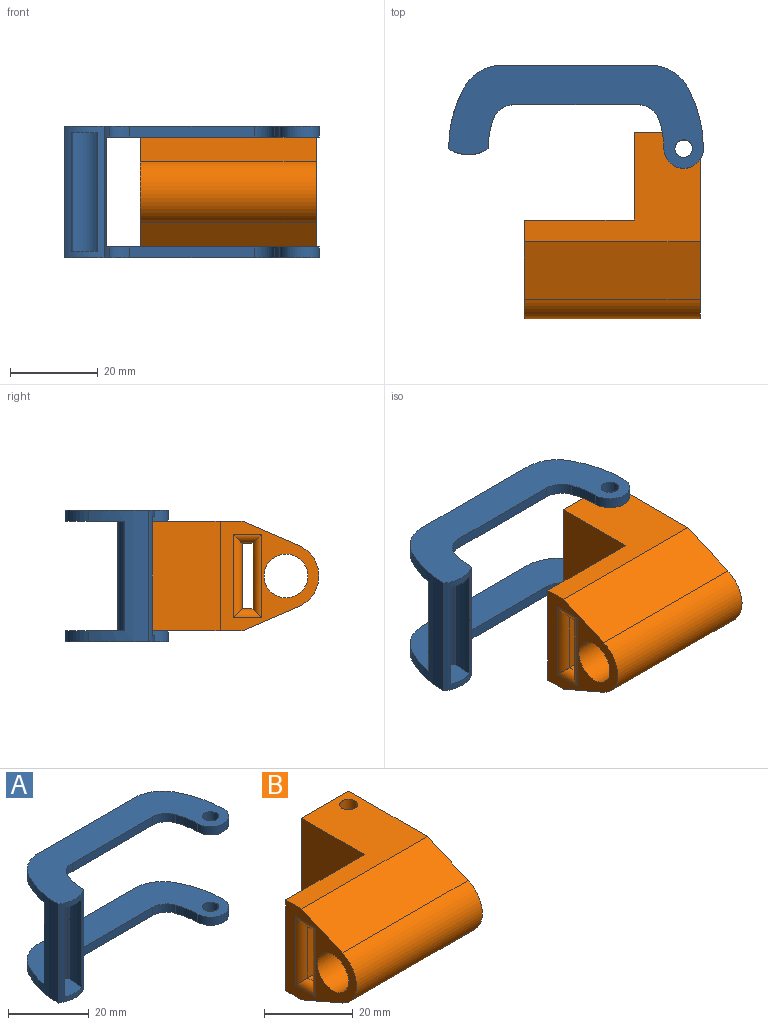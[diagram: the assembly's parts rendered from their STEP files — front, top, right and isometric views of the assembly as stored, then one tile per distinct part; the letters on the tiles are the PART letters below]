
ASSEMBLY  parts=2 mates=1
PART A: 33 faces, bbox 58x23.5x30 mm
  f0: cylinder r=8mm len=30mm, axis (0,0,-1), area 120.6mm2, adj f4,f7,f8,f12,f29,f30,f31,f32
  f1: cylinder r=6mm len=25mm, axis (0,0,-1), area 255.4mm2, adj f2,f7,f8,f19
  f2: plane 57.47x23.5mm, normal (0,0,1), area 591mm2, adj f1,f3,f5,f6,f7,f8,f9,f10
  f3: cylinder r=2mm len=4mm, axis (0,0,-1), area 31.4mm2, adj f2,f4
  f4: plane 58x23.5mm, normal (0,0,-1), area 656.9mm2, adj f0,f3,f5,f6,f7,f8,f9,f10
  f5: cylinder r=20mm len=6.67mm, axis (0,0,-1), area 17mm2, adj f2,f4,f11,f25
  f6: plane 28.28x2.5mm, normal (0,-1,0), area 70.7mm2, adj f2,f4,f24,f25
  f7: cylinder r=20mm len=30mm, axis (0,0,-1), area 143.6mm2, adj f0,f1,f2,f4,f12,f19,f24,f26
  f8: cylinder r=29mm len=30mm, axis (0,0,-1), area 209.8mm2, adj f0,f1,f2,f4,f12,f19,f21,f23
  f9: plane 33.47x2.5mm, normal (0,1,0), area 83.7mm2, adj f2,f4,f20,f21
  f10: cylinder r=29mm len=13.74mm, axis (0,0,-1), area 35.8mm2, adj f2,f4,f11,f20
  f11: cylinder r=4.5mm len=9mm, axis (0,0,-1), area 35.3mm2, adj f2,f4,f5,f10
  f12: plane 58x23.5mm, normal (0,0,1), area 656.9mm2, adj f0,f7,f8,f13,f14,f15,f16,f17
  f13: cylinder r=4.5mm len=9mm, axis (0,0,-1), area 35.3mm2, adj f12,f14,f18,f19
  f14: cylinder r=29mm len=13.74mm, axis (0,0,-1), area 35.8mm2, adj f12,f13,f19,f22
  f15: plane 33.47x2.5mm, normal (0,1,0), area 83.7mm2, adj f12,f19,f22,f23
  f16: plane 28.28x2.5mm, normal (0,-1,0), area 70.7mm2, adj f12,f19,f26,f27
  f17: cylinder r=2mm len=4mm, axis (0,0,-1), area 31.4mm2, adj f12,f19
  f18: cylinder r=20mm len=6.67mm, axis (0,0,-1), area 17mm2, adj f12,f13,f19,f27
  f19: plane 57.47x23.5mm, normal (0,0,-1), area 591mm2, adj f1,f7,f8,f13,f14,f15,f16,f17
  f20: cylinder r=10mm len=8.81mm, axis (0,0,-1), area 26.9mm2, adj f2,f4,f9,f10
  f21: cylinder r=10mm len=8.81mm, axis (0,0,-1), area 26.9mm2, adj f2,f4,f8,f9
  f22: cylinder r=10mm len=8.81mm, axis (0,0,-1), area 26.9mm2, adj f12,f14,f15,f19
  f23: cylinder r=10mm len=8.81mm, axis (0,0,-1), area 26.9mm2, adj f8,f12,f15,f19
  f24: cylinder r=5mm len=4.71mm, axis (0,0,-1), area 15.4mm2, adj f2,f4,f6,f7
  f25: cylinder r=5mm len=4.71mm, axis (0,0,-1), area 15.4mm2, adj f2,f4,f5,f6
  f26: cylinder r=5mm len=4.71mm, axis (0,0,-1), area 15.4mm2, adj f7,f12,f16,f19
  f27: cylinder r=5mm len=4.71mm, axis (0,0,-1), area 15.4mm2, adj f12,f16,f18,f19
  f28: cylinder r=4.5mm len=27mm, axis (0,0,-1), area 177.7mm2, adj f29,f30,f31,f32
  f29: plane 6.89x6.37mm, normal (0,0,1), area 38mm2, adj f0,f28,f30,f31
  f30: cylinder r=21.5mm len=27mm, axis (0,0,-1), area 129.6mm2, adj f0,f28,f29,f32
  f31: cylinder r=27.5mm len=27mm, axis (0,0,-1), area 148.6mm2, adj f0,f28,f29,f32
  f32: plane 6.89x6.37mm, normal (0,0,-1), area 38mm2, adj f0,f28,f30,f31
PART B: 24 faces, bbox 40x42.5x25 mm
  f0: plane 42.5x25mm, normal (1,0,0), area 430.4mm2, adj f1,f5,f6,f7,f8,f9,f10,f12
  f1: plane 25x15mm, normal (0,1,0), area 180mm2, adj f0,f4,f5,f6,f12,f14,f19
  f2: plane 25x22.5mm, normal (-1,0,0), area 219.4mm2, adj f3,f5,f6,f7,f8,f9,f10,f20
  f3: plane 25x25mm, normal (0,1,0), area 625mm2, adj f2,f4,f5,f6
  f4: plane 25x20mm, normal (-1,0,0), area 500mm2, adj f1,f3,f5,f6
  f5: plane 40x25mm, normal (0,0,1), area 487.4mm2, adj f0,f1,f2,f3,f4,f7,f18
  f6: plane 40x25mm, normal (0,0,-1), area 487.4mm2, adj f0,f1,f2,f3,f4,f10,f17
  f7: plane 40x12.98mm, normal (0,-0.4,0.92), area 565.7mm2, adj f0,f2,f5,f8
  f8: cylinder r=7.5mm len=40mm, axis (1,0,0), area 697.4mm2, adj f0,f2,f7,f10
  f9: cylinder r=5mm len=40mm, axis (1,0,0), area 1256.6mm2, adj f0,f2
  f10: plane 40x12.98mm, normal (0,-0.4,-0.92), area 565.7mm2, adj f0,f2,f6,f8
  f11: plane 25x15mm, normal (0,-1,0), area 375mm2, adj f12,f14,f16,f20
  f12: plane 38x27.5mm, normal (0,0,-1), area 336.3mm2, adj f0,f1,f11,f13,f15,f16,f18,f19
  f13: plane 38x15mm, normal (0,1,0), area 570mm2, adj f0,f12,f14,f23
  f14: plane 38x27.5mm, normal (0,0,1), area 336.3mm2, adj f0,f1,f11,f13,f15,f16,f17,f19
  f15: plane 19x15mm, normal (1,0,0), area 285mm2, adj f12,f14,f16,f19
  f16: cylinder r=3mm len=15mm, axis (0,0,-1), area 70.7mm2, adj f11,f12,f14,f15
  f17: cylinder r=2mm len=5mm, axis (0,0,1), area 62.8mm2, adj f6,f14
  f18: cylinder r=2mm len=5mm, axis (0,0,1), area 62.8mm2, adj f5,f12
  f19: cylinder r=3mm len=15mm, axis (0,0,-1), area 70.7mm2, adj f1,f12,f14,f15
  f20: cylinder r=2mm len=19mm, axis (0,0,-1), area 51.7mm2, adj f2,f11,f21,f22
  f21: cylinder r=2mm len=6.5mm, axis (0,1,0), area 12.4mm2, adj f2,f12,f20,f23
  f22: cylinder r=2mm len=6.5mm, axis (0,-1,0), area 12.4mm2, adj f2,f14,f20,f23
  f23: cylinder r=2mm len=19mm, axis (0,0,1), area 51.7mm2, adj f2,f13,f21,f22
PLACE A t=(21.57,24.66,-16.37)mm
PLACE B t=(-14.68,8.41,-13.87)mm
MATE cylindrical B.f17 <-> A.f3  axis (0,0,-1) through (21.57,24.66,-13.87)mm
